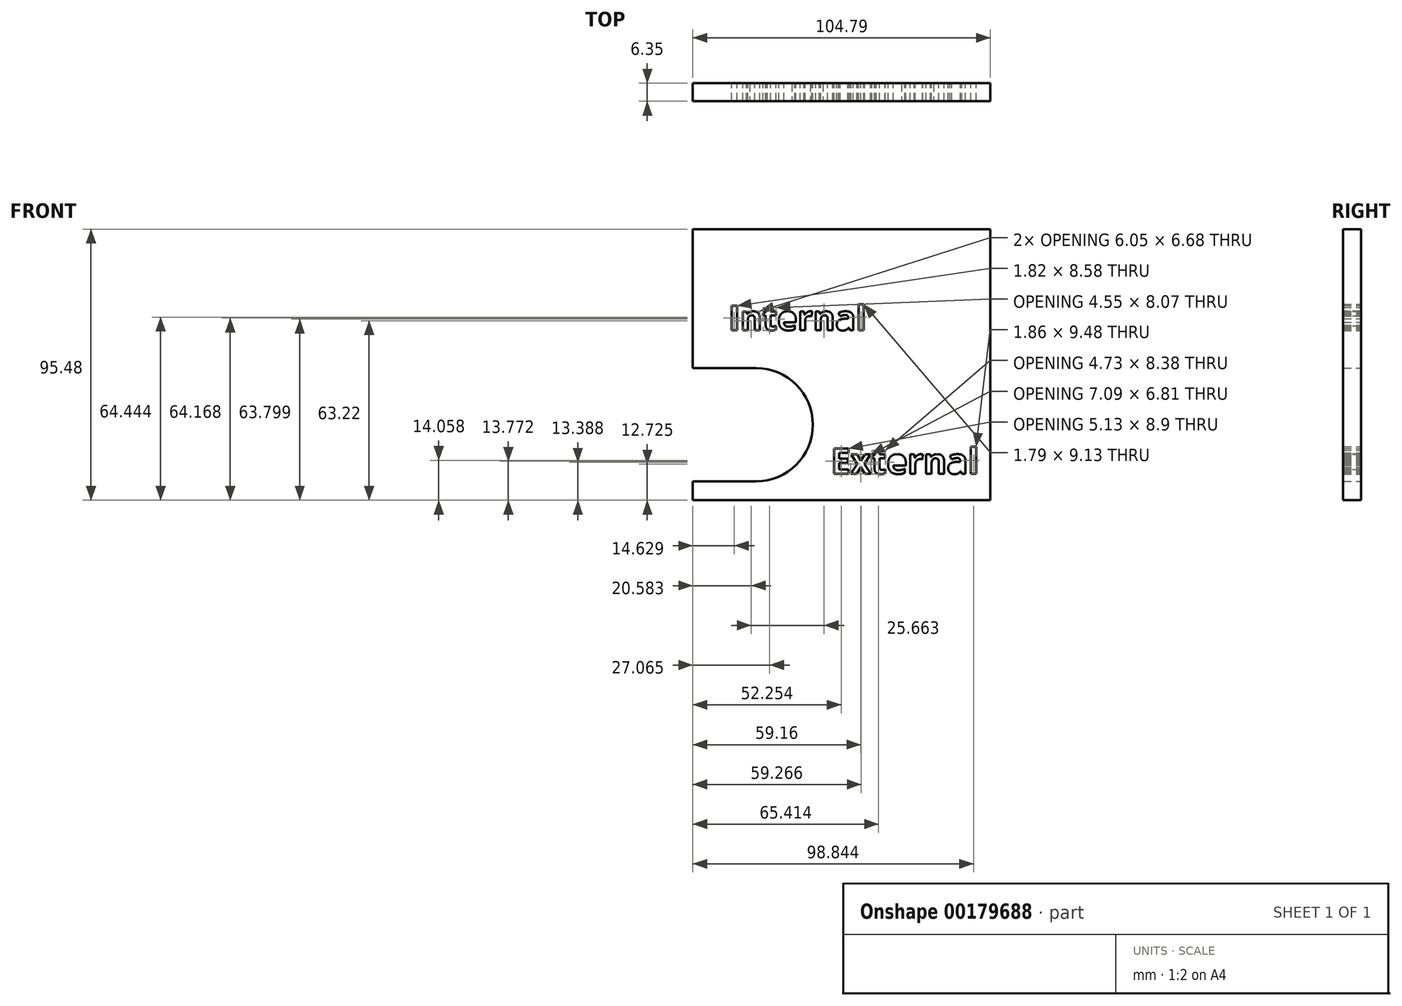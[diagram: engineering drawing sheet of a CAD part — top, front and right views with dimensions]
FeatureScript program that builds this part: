
annotation { "Feature Type Name" : "Feature", "Feature Type Description" : "" }
export const myFeature = defineFeature(function(context is Context, id is Id, definition is map)
    precondition{}
    {
        {
            var Q0;
            Q0=qCreatedBy(makeId("Front.planeOp"),FACE);
            var sketch = newSketch(context, id + "F0", { "sketchPlane" : qUnion([Q0])});
            skLineSegment(sketch, "E0", {"start": v(46.24, -34.1) * mm, "end": v(46.24, 61.38) * mm});
            skLineSegment(sketch, "E1", {"start": v(46.24, 61.38) * mm, "end": v(-58.55, 61.38) * mm});
            skLineSegment(sketch, "E2", {"start": v(-58.55, 61.38) * mm, "end": v(-58.55, 12.48) * mm});
            skLineSegment(sketch, "E3", {"start": v(46.24, -34.1) * mm, "end": v(-58.55, -34.1) * mm});
            skLineSegment(sketch, "E4", {"start": v(-58.55, 12.48) * mm, "end": v(-36.26, 12.48) * mm});
            skLineSegment(sketch, "E5", {"start": v(-58.55, -34.1) * mm, "end": v(-58.55, -27.45) * mm});
            skLineSegment(sketch, "E6", {"start": v(-58.55, -27.45) * mm, "end": v(-36.26, -27.45) * mm});
            skArc(sketch, "E7", {"start": v(-36.26, -27.45) * mm, "mid": v(-16.3, -7.49) * mm, "end": v(-36.26, 12.48) * mm});
            skText(sketch, "E8", { "text": "Internal", "fontName": "OpenSans-Bold.ttf"});
            skText(sketch, "E9", { "text": "External", "fontName": "OpenSans-Bold.ttf"});
            const initialGuessF0  = {"E8": [-0.04591, 0.02578, 1, 0, 0.00865], "E9": [-0.00998, -0.02478, 1, 0, 0.00898]};
            skSetInitialGuess(sketch, initialGuessF0);
            skSolve(sketch);
        }
        {
            var Q0;
            Q0 = qSketchRegion(id + "F0", true);
            extrude(context, id + "F1", {"entities" : qUnion([Q0]), "depth" : 6.35 * mm});
        }
    });
